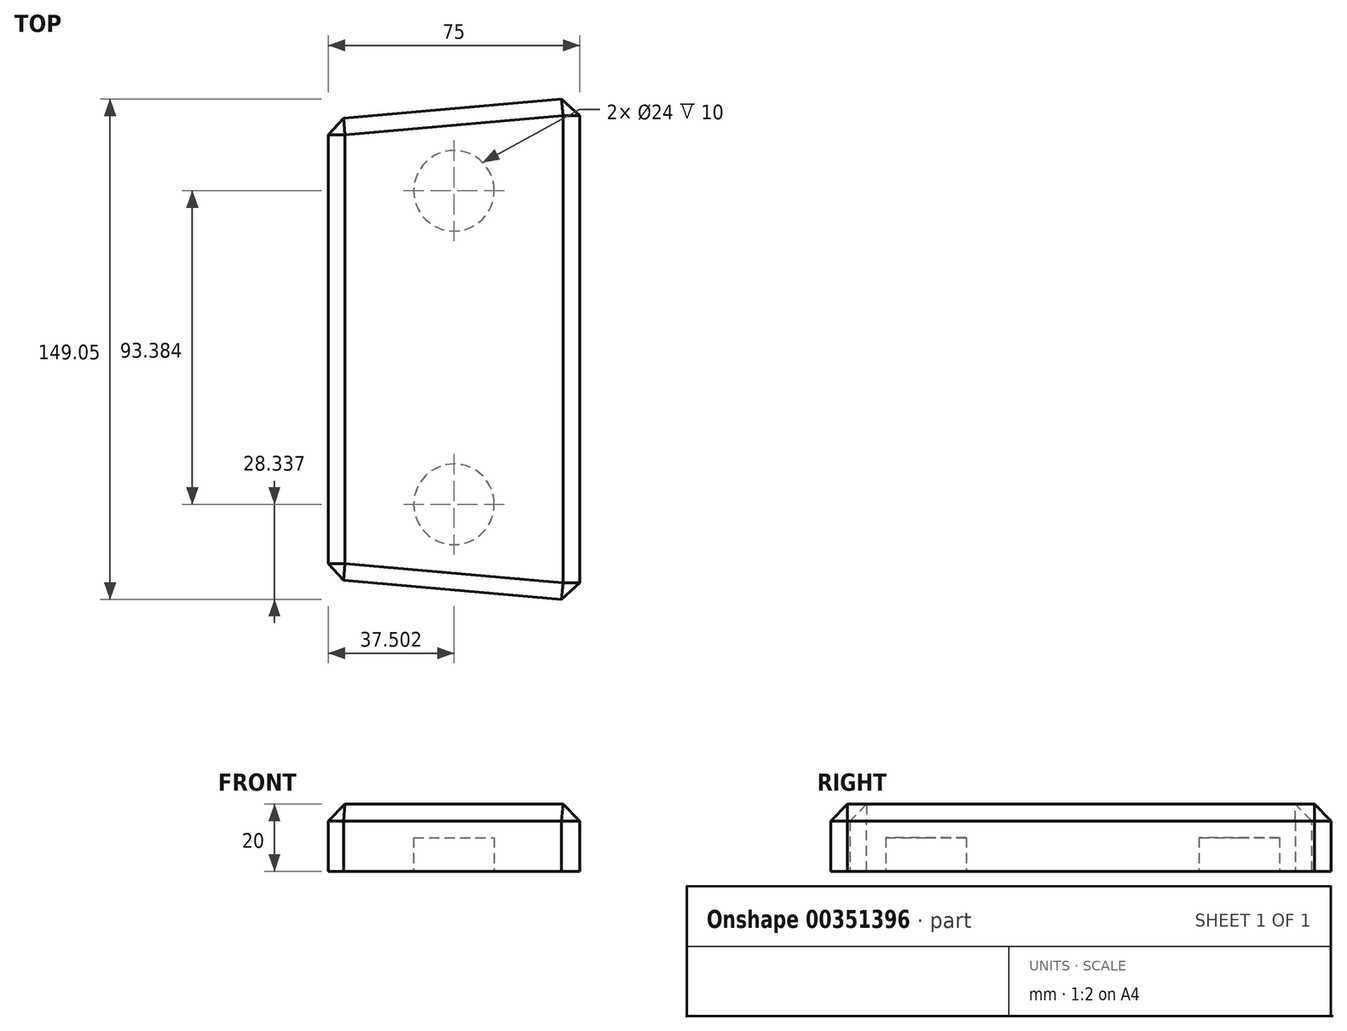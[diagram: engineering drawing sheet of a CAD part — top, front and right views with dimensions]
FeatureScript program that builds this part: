
annotation { "Feature Type Name" : "Feature", "Feature Type Description" : "" }
export const myFeature = defineFeature(function(context is Context, id is Id, definition is map)
    precondition{}
    {
        {
            var Q0;
            Q0=qCreatedBy(makeId("Top.planeOp"),FACE);
            var sketch = newSketch(context, id + "F0", { "sketchPlane" : qUnion([Q0])});
            skLineSegment(sketch, "E0", {"start": v(-67.14, 72.62) * mm, "end": v(7.86, 79.18) * mm});
            skLineSegment(sketch, "E1", {"start": v(7.86, 79.18) * mm, "end": v(7.86, -70.82) * mm});
            skLineSegment(sketch, "E2", {"start": v(7.86, -70.82) * mm, "end": v(-67.14, -64.26) * mm});
            skLineSegment(sketch, "E3", {"start": v(-67.14, 72.62) * mm, "end": v(-67.14, -64.26) * mm});
            skPoint(sketch, "E4.visualSharp", {"position": v(7.86, 79.18) * mm});
            skPoint(sketch, "E5.visualSharp", {"position": v(-67.14, 72.62) * mm});
            skPoint(sketch, "E6.visualSharp", {"position": v(7.86, -70.82) * mm});
            skPoint(sketch, "E7.visualSharp", {"position": v(-67.14, -64.26) * mm});
            skSolve(sketch);
        }
        {
            var Q0;
            Q0=makeQuery(id+"F0.imprint","IMPRINT",FACE,{"disambiguationData":[TD([[makeQuery(id+"F0.imprint","IMPRINT",EDGE,{"derivedFrom":sQuery(id+"F0.wireOp",EDGE,"E0")}),-1.0]])]});
            extrude(context, id + "F1", {"entities" : qUnion([Q0]), "endBound" : BoundingType.SYMMETRIC, "depth" : 20 * mm});
        }
        {
            var Q0;
            Q0=makeQuery(id+"F1.opExtrude","SWEPT_EDGE",EDGE,{"disambiguationData":[OSD([sQuery(id+"F0.wireOp",EDGE,"E0"),sQuery(id+"F0.wireOp",EDGE,"E3")])]});
            var Q1;
            Q1=makeQuery(id+"F1.opExtrude","CAP_EDGE",EDGE,{"disambiguationData":[OSD([sQuery(id+"F0.wireOp",EDGE,"E0")])],"isStart":false});
            var Q2;
            Q2=makeQuery(id+"F1.opExtrude","CAP_EDGE",EDGE,{"disambiguationData":[OSD([sQuery(id+"F0.wireOp",EDGE,"E3")])],"isStart":false});
            var Q3;
            Q3=makeQuery(id+"F1.opExtrude","SWEPT_EDGE",EDGE,{"disambiguationData":[OSD([sQuery(id+"F0.wireOp",EDGE,"E0"),sQuery(id+"F0.wireOp",EDGE,"E1")])]});
            var Q4;
            Q4=makeQuery(id+"F1.opExtrude","CAP_EDGE",EDGE,{"disambiguationData":[OSD([sQuery(id+"F0.wireOp",EDGE,"E1")])],"isStart":false});
            var Q5;
            Q5=makeQuery(id+"F1.opExtrude","SWEPT_EDGE",EDGE,{"disambiguationData":[OSD([sQuery(id+"F0.wireOp",EDGE,"E1"),sQuery(id+"F0.wireOp",EDGE,"E2")])]});
            var Q6;
            Q6=makeQuery(id+"F1.opExtrude","CAP_EDGE",EDGE,{"disambiguationData":[OSD([sQuery(id+"F0.wireOp",EDGE,"E2")])],"isStart":false});
            var Q7;
            Q7=makeQuery(id+"F1.opExtrude","SWEPT_EDGE",EDGE,{"disambiguationData":[OSD([sQuery(id+"F0.wireOp",EDGE,"E2"),sQuery(id+"F0.wireOp",EDGE,"E3")])]});
            chamfer(context, id + "F2", {"entities" : qUnion([Q0, Q1, Q2, Q3, Q4, Q5, Q6, Q7]), "width" : 5 * mm, "tangentPropagation" : true});
        }
        {
            var Q0;
            Q0=makeQuery(id+"F1.opExtrude","CAP_FACE",FACE,{"disambiguationData":[OSD([sQuery(id+"F0.wireOp",EDGE,"E0"),sQuery(id+"F0.wireOp",EDGE,"E1"),sQuery(id+"F0.wireOp",EDGE,"E2"),sQuery(id+"F0.wireOp",EDGE,"E3")])],"isStart":true});
            var sketch = newSketch(context, id + "F3", { "sketchPlane" : qUnion([Q0])});
            skCircle(sketch, "E8", {"center": v(-29.64, 42.01) * mm, "radius": 12 * mm});
            skCircle(sketch, "E9", {"center": v(-29.64, -51.37) * mm, "radius": 12 * mm});
            skSolve(sketch);
        }
        {
            var Q0;
            Q0=makeQuery(id+"F3.imprint","IMPRINT",FACE,{"disambiguationData":[TD([[makeQuery(id+"F3.imprint","IMPRINT",EDGE,{"derivedFrom":sQuery(id+"F3.wireOp",EDGE,"E8")}),1.0]])]});
            var Q1;
            Q1=makeQuery(id+"F3.imprint","IMPRINT",FACE,{"disambiguationData":[TD([[makeQuery(id+"F3.imprint","IMPRINT",EDGE,{"derivedFrom":sQuery(id+"F3.wireOp",EDGE,"E9")}),1.0]])]});
            var Q2;
            Q2=sQuery(id+"F3.wireOp",EDGE,"E8");
            var Q3;
            Q3=sQuery(id+"F3.wireOp",EDGE,"E9");
            extrude(context, id + "F4", {"entities" : qUnion([Q0, Q1]), "operationType" : NewBodyOperationType.REMOVE, "surfaceEntities" : qUnion([Q2, Q3]), "oppositeDirection" : true, "depth" : 10 * mm});
        }
    });
